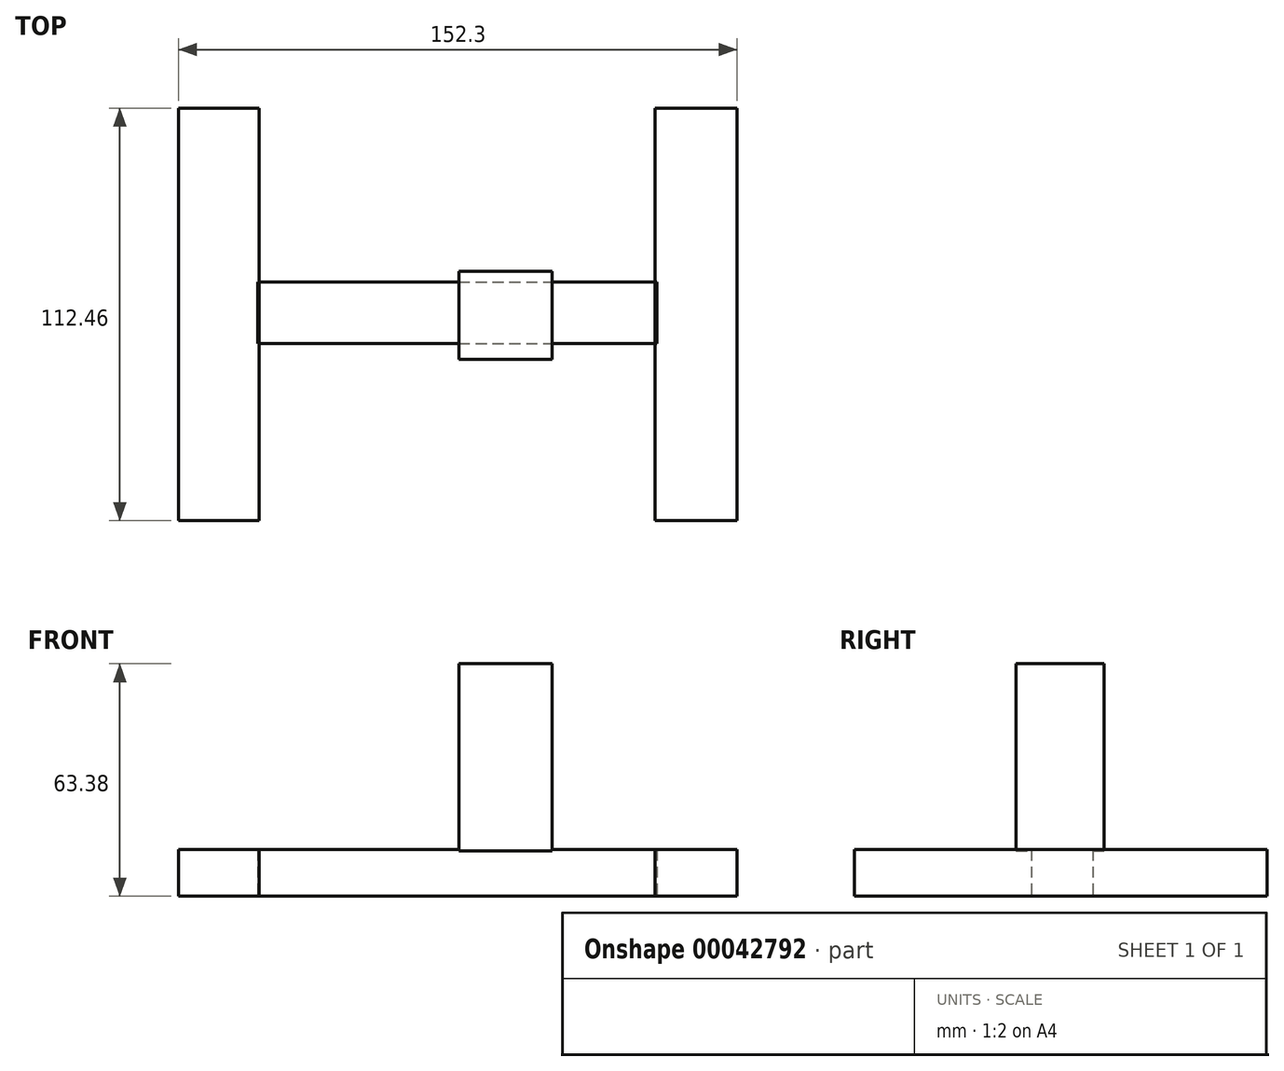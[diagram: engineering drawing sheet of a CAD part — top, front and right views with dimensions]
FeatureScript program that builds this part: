
annotation { "Feature Type Name" : "Feature", "Feature Type Description" : "" }
export const myFeature = defineFeature(function(context is Context, id is Id, definition is map)
    precondition{}
    {
        {
            var Q0;
            Q0=qCreatedBy(makeId("Top.planeOp"),FACE);
            var sketch = newSketch(context, id + "F0", { "sketchPlane" : qUnion([Q0])});
            skLineSegment(sketch, "E0.bottom", {"start": v(-76.4, 56.23) * mm, "end": v(-54.5, 56.23) * mm});
            skLineSegment(sketch, "E0.top", {"start": v(-76.4, -56.23) * mm, "end": v(-54.5, -56.23) * mm});
            skLineSegment(sketch, "E0.left", {"start": v(-76.4, 56.23) * mm, "end": v(-76.4, -56.23) * mm});
            skLineSegment(sketch, "E0.right", {"start": v(-54.5, 56.23) * mm, "end": v(-54.5, -56.23) * mm});
            skLineSegment(sketch, "E1.bottom", {"start": v(53.46, 56.23) * mm, "end": v(75.9, 56.23) * mm});
            skLineSegment(sketch, "E1.top", {"start": v(53.46, -56.23) * mm, "end": v(75.9, -56.23) * mm});
            skLineSegment(sketch, "E1.left", {"start": v(53.46, 56.23) * mm, "end": v(53.46, -56.23) * mm});
            skLineSegment(sketch, "E1.right", {"start": v(75.9, 56.23) * mm, "end": v(75.9, -56.23) * mm});
            skSolve(sketch);
        }
        {
            var Q0;
            Q0=makeQuery(id+"F0.imprint","IMPRINT",FACE,{"disambiguationData":[TD([[makeQuery(id+"F0.imprint","IMPRINT",EDGE,{"derivedFrom":sQuery(id+"F0.wireOp",EDGE,"E0.bottom")}),-1.0]])]});
            var Q1;
            Q1=makeQuery(id+"F0.imprint","IMPRINT",FACE,{"disambiguationData":[TD([[makeQuery(id+"F0.imprint","IMPRINT",EDGE,{"derivedFrom":sQuery(id+"F0.wireOp",EDGE,"E1.bottom")}),-1.0]])]});
            extrude(context, id + "F1", {"entities" : qUnion([Q0, Q1]), "depth" : 12.7 * mm});
        }
        {
            var Q0;
            Q0=qCreatedBy(makeId("Top.planeOp"),FACE);
            var sketch = newSketch(context, id + "F2", { "sketchPlane" : qUnion([Q0])});
            skLineSegment(sketch, "E2.bottom", {"start": v(-54.88, 8.8) * mm, "end": v(53.97, 8.8) * mm});
            skLineSegment(sketch, "E2.top", {"start": v(-54.88, -7.98) * mm, "end": v(53.97, -7.98) * mm});
            skLineSegment(sketch, "E2.left", {"start": v(-54.88, 8.8) * mm, "end": v(-54.88, -7.98) * mm});
            skLineSegment(sketch, "E2.right", {"start": v(53.97, 8.8) * mm, "end": v(53.97, -7.98) * mm});
            skSolve(sketch);
        }
        {
            var Q0;
            Q0=makeQuery(id+"F2.imprint","IMPRINT",FACE,{"disambiguationData":[TD([[makeQuery(id+"F2.imprint","IMPRINT",EDGE,{"derivedFrom":sQuery(id+"F2.wireOp",EDGE,"E2.bottom")}),-1.0]])]});
            extrude(context, id + "F3", {"entities" : qUnion([Q0]), "depth" : 12.7 * mm});
        }
        {
            var Q0;
            Q0=qCreatedBy(makeId("Right.planeOp"),FACE);
            var sketch = newSketch(context, id + "F4", { "sketchPlane" : qUnion([Q0])});
            skLineSegment(sketch, "E3.bottom", {"start": v(-12.2, 63.38) * mm, "end": v(11.79, 63.38) * mm});
            skLineSegment(sketch, "E3.top", {"start": v(-12.2, 12.4) * mm, "end": v(11.79, 12.4) * mm});
            skLineSegment(sketch, "E3.left", {"start": v(-12.2, 63.38) * mm, "end": v(-12.2, 12.4) * mm});
            skLineSegment(sketch, "E3.right", {"start": v(11.79, 63.38) * mm, "end": v(11.79, 12.4) * mm});
            skSolve(sketch);
        }
        {
            var Q0;
            Q0 = qSketchRegion(id + "F4", true);
            extrude(context, id + "F5", {"entities" : qUnion([Q0]), "operationType" : NewBodyOperationType.ADD, "depth" : 25.4 * mm});
        }
    });
